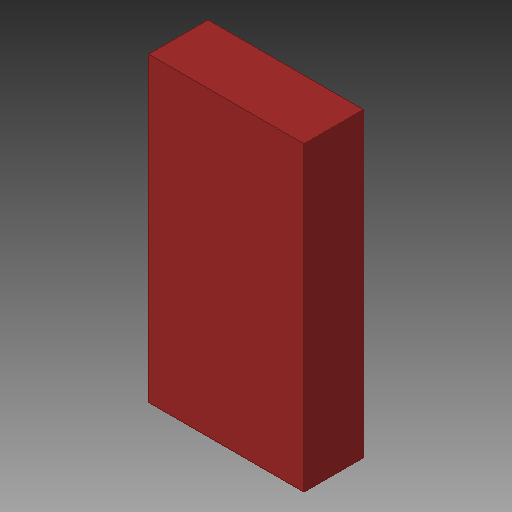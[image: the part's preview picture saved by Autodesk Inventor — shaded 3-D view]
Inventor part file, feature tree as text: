
AUTODESK INVENTOR PART (.ipt)
format: ipt  version: 2018 (Build 220112000, 112)  size: 79,872 bytes
history: native  units: in
note: dims shown in document units (in); Inventor stores cm internally (conversion verified against a paired STEP export)
features: other x1, extrude x1
ambient origin geometry x8: Origin, YZ Plane, XZ Plane, XY Plane, X Axis, Y Axis, Z Axis, Center Point
bodies: Solid1 (feature_tree)
feature tree (2):
  other  "JP1M, SBW_NC_69"
  extrude  "Extrusion1"  Depth=0.0394in TaperAngle=0.0deg
